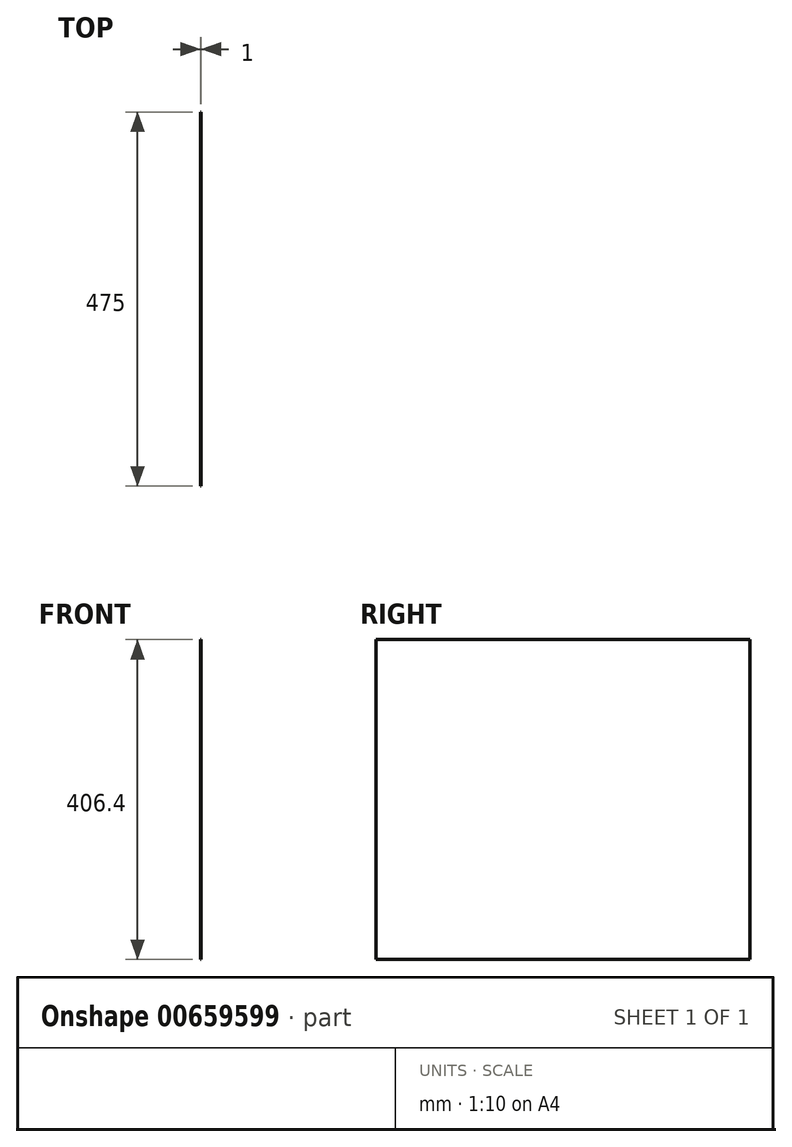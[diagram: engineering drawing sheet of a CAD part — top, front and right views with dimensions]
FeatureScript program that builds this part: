
annotation { "Feature Type Name" : "Feature", "Feature Type Description" : "" }
export const myFeature = defineFeature(function(context is Context, id is Id, definition is map)
    precondition{}
    {
        {
            var Q0;
            Q0=qCreatedBy(makeId("Right.planeOp"),FACE);
            var sketch = newSketch(context, id + "F0", { "sketchPlane" : qUnion([Q0])});
            skLineSegment(sketch, "E0.bottom", {"start": v(237.5, -203.2) * mm, "end": v(-237.5, -203.2) * mm});
            skLineSegment(sketch, "E0.top", {"start": v(237.5, 203.2) * mm, "end": v(-237.5, 203.2) * mm});
            skLineSegment(sketch, "E0.left", {"start": v(237.5, -203.2) * mm, "end": v(237.5, 203.2) * mm});
            skLineSegment(sketch, "E0.right", {"start": v(-237.5, -203.2) * mm, "end": v(-237.5, 203.2) * mm});
            skPoint(sketch, "E0.middle", {"position": v(0, 0) * mm});
            skSolve(sketch);
        }
        {
            var Q0;
            Q0=qSketchRegion(id+"F0",true);
            extrude(context, id + "F1", {"entities" : qUnion([Q0]), "depth" : 1 * mm, "offsetDistance" : 25 * mm});
        }
    });
